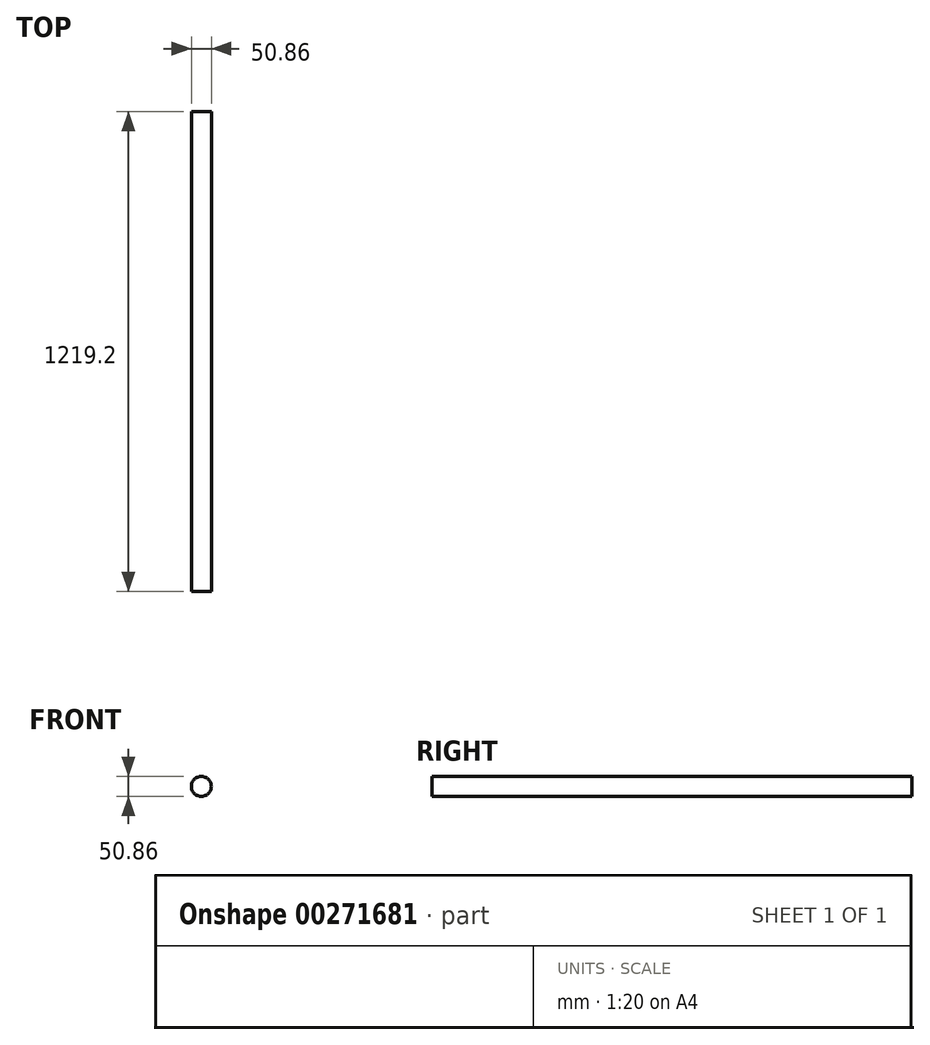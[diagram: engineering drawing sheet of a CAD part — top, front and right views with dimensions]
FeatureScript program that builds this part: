
annotation { "Feature Type Name" : "Feature", "Feature Type Description" : "" }
export const myFeature = defineFeature(function(context is Context, id is Id, definition is map)
    precondition{}
    {
        {
            var Q0;
            Q0=qCreatedBy(makeId("Front.planeOp"),FACE);
            var sketch = newSketch(context, id + "F0", { "sketchPlane" : qUnion([Q0])});
            skCircle(sketch, "E0", {"center": v(0, 0) * mm, "radius": 25.43 * mm});
            skSolve(sketch);
        }
        {
            var Q0;
            Q0=makeQuery(id+"F0.imprint","IMPRINT",FACE,{"disambiguationData":[TD([[makeQuery(id+"F0.imprint","IMPRINT",EDGE,{"derivedFrom":sQuery(id+"F0.wireOp",EDGE,"E0")}),1.0]])]});
            extrude(context, id + "F1", {"entities" : qUnion([Q0]), "depth" : 1219.2 * mm});
        }
    });
